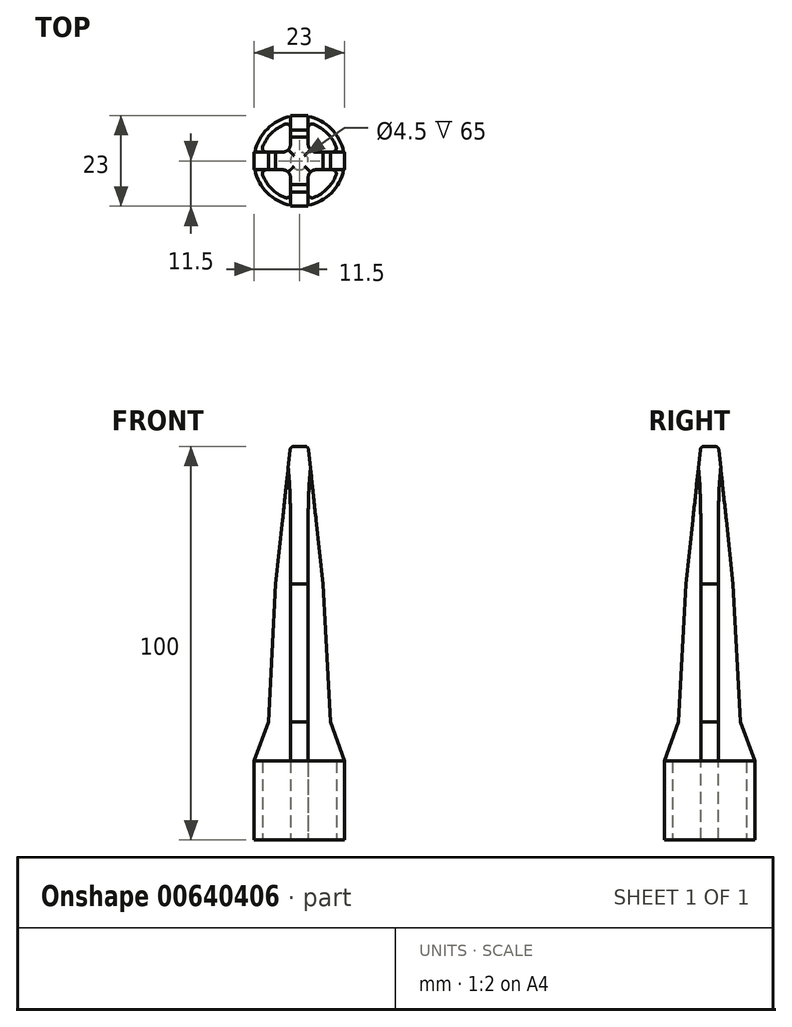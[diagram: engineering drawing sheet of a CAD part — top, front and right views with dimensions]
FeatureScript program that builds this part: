
annotation { "Feature Type Name" : "Feature", "Feature Type Description" : "" }
export const myFeature = defineFeature(function(context is Context, id is Id, definition is map)
    precondition{}
    {
        {
            var Q0;
            Q0=qCreatedBy(makeId("Top.planeOp"),FACE);
            var sketch = newSketch(context, id + "F0", { "sketchPlane" : qUnion([Q0])});
            skCircle(sketch, "E0", {"center": v(0, 0) * mm, "radius": 11.5 * mm});
            skCircle(sketch, "E1", {"center": v(0, 0) * mm, "radius": 2.25 * mm});
            skLineSegment(sketch, "E2", {"start": v(-2.25, 2.25) * mm, "end": v(-2.25, 9.74) * mm});
            skLineSegment(sketch, "E3", {"start": v(2.25, 2.25) * mm, "end": v(2.25, 9.74) * mm});
            skLineSegment(sketch, "E4", {"start": v(2.25, 2.25) * mm, "end": v(9.74, 2.25) * mm});
            skLineSegment(sketch, "E5", {"start": v(2.25, -2.25) * mm, "end": v(9.74, -2.25) * mm});
            skLineSegment(sketch, "E6.MirrorCS", {"start": v(-2.25, -2.25) * mm, "end": v(-2.25, -9.74) * mm});
            skLineSegment(sketch, "E7.MirrorCS", {"start": v(2.25, -2.25) * mm, "end": v(2.25, -9.74) * mm});
            skLineSegment(sketch, "E8.MirrorCS", {"start": v(-2.25, 2.25) * mm, "end": v(-9.74, 2.25) * mm});
            skLineSegment(sketch, "E9.MirrorCS", {"start": v(-2.25, -2.25) * mm, "end": v(-9.74, -2.25) * mm});
            skArc(sketch, "E10", {"start": v(-9.74, -2.25) * mm, "mid": v(0, -10) * mm, "end": v(9.74, -2.25) * mm});
            skPoint(sketch, "E11.orphan", {"position": v(-2.25, 11.28) * mm});
            skPoint(sketch, "E12.orphan", {"position": v(2.25, 11.28) * mm});
            skPoint(sketch, "E13.orphan", {"position": v(-11.28, 2.25) * mm});
            skPoint(sketch, "E14.orphan", {"position": v(-11.28, -2.25) * mm});
            skPoint(sketch, "E15.orphan", {"position": v(-2.25, -11.28) * mm});
            skPoint(sketch, "E16.orphan", {"position": v(2.25, -11.28) * mm});
            skPoint(sketch, "E17.orphan", {"position": v(11.28, -2.25) * mm});
            skPoint(sketch, "E18.orphan", {"position": v(11.28, 2.25) * mm});
            skArc(sketch, "E19.trimOffspring", {"start": v(9.74, 2.25) * mm, "mid": v(0, 10) * mm, "end": v(-9.74, 2.25) * mm});
            skPoint(sketch, "E20.orphan", {"position": v(-2.25, 0) * mm});
            skPoint(sketch, "E21.orphan", {"position": v(0, 2.25) * mm});
            skPoint(sketch, "E22.orphan", {"position": v(2.25, 0) * mm});
            skPoint(sketch, "E23.orphan", {"position": v(0, -2.25) * mm});
            skSolve(sketch);
        }
        {
            var Q0;
            Q0 = qSketchRegion(id + "F0", true);
            extrude(context, id + "F1", {"entities" : qUnion([Q0]), "depth" : 65 * mm, "offsetDistance" : 25 * mm});
        }
        {
            var Q0;
            Q0=makeQuery(id+"F1.opExtrude","CAP_FACE",FACE,{"disambiguationData":[OSD([sQuery(id+"F0.wireOp",EDGE,"E0"),sQuery(id+"F0.wireOp",EDGE,"E1"),sQuery(id+"F0.wireOp",EDGE,"E2"),sQuery(id+"F0.wireOp",EDGE,"E3"),sQuery(id+"F0.wireOp",EDGE,"E4"),sQuery(id+"F0.wireOp",EDGE,"E5"),sQuery(id+"F0.wireOp",EDGE,"E6.MirrorCS"),sQuery(id+"F0.wireOp",EDGE,"E7.MirrorCS"),sQuery(id+"F0.wireOp",EDGE,"E8.MirrorCS"),sQuery(id+"F0.wireOp",EDGE,"E9.MirrorCS"),sQuery(id+"F0.wireOp",EDGE,"E10"),sQuery(id+"F0.wireOp",EDGE,"E19.trimOffspring")])],"isStart":false});
            var sketch = newSketch(context, id + "F2", { "sketchPlane" : qUnion([Q0])});
            skLineSegment(sketch, "E24.0", {"start": v(-2.25, 2.25) * mm, "end": v(-2.25, 6) * mm});
            skLineSegment(sketch, "E25.0", {"start": v(-2.25, 2.25) * mm, "end": v(-6, 2.25) * mm});
            skLineSegment(sketch, "E26.0", {"start": v(-2.25, -2.25) * mm, "end": v(-6, -2.25) * mm});
            skLineSegment(sketch, "E27.0", {"start": v(2.25, 2.25) * mm, "end": v(2.25, 6) * mm});
            skLineSegment(sketch, "E28.0", {"start": v(2.25, -2.25) * mm, "end": v(6, -2.25) * mm});
            skLineSegment(sketch, "E28.1", {"start": v(2.25, -2.25) * mm, "end": v(2.25, -6) * mm});
            skLineSegment(sketch, "E28.2", {"start": v(2.25, 2.25) * mm, "end": v(6, 2.25) * mm});
            skLineSegment(sketch, "E28.3", {"start": v(-2.25, -2.25) * mm, "end": v(-2.25, -6) * mm});
            skLineSegment(sketch, "E29", {"start": v(-2.25, 6) * mm, "end": v(2.25, 6) * mm});
            skLineSegment(sketch, "E30", {"start": v(-6, 2.25) * mm, "end": v(-6, -2.25) * mm});
            skLineSegment(sketch, "E31", {"start": v(-2.25, -6) * mm, "end": v(2.25, -6) * mm});
            skLineSegment(sketch, "E32", {"start": v(6, 2.25) * mm, "end": v(6, -2.25) * mm});
            skPoint(sketch, "E33.orphan", {"position": v(-9.74, 2.25) * mm});
            skPoint(sketch, "E34.orphan", {"position": v(-9.74, -2.25) * mm});
            skPoint(sketch, "E35.orphan", {"position": v(2.25, -9.74) * mm});
            skPoint(sketch, "E36.orphan", {"position": v(-2.25, -9.74) * mm});
            skPoint(sketch, "E37.orphan", {"position": v(9.74, -2.25) * mm});
            skPoint(sketch, "E38.orphan", {"position": v(9.74, 2.25) * mm});
            skPoint(sketch, "E39.orphan", {"position": v(2.25, 9.74) * mm});
            skPoint(sketch, "E40.orphan", {"position": v(-2.25, 9.74) * mm});
            skSolve(sketch);
        }
        {
            var Q0;
            Q0 = qSketchRegion(id + "F2", true);
            extrude(context, id + "F3", {"entities" : qUnion([Q0]), "operationType" : NewBodyOperationType.ADD, "depth" : 35 * mm, "offsetDistance" : 25 * mm});
        }
        {
            var Q0;
            Q0=makeQuery(id+"F3.boolean.opBoolean","MERGE",FACE,{"derivedFrom":[makeQuery(id+"F1.opExtrude","SWEPT_FACE",FACE,{"disambiguationData":[OSD([sQuery(id+"F0.wireOp",EDGE,"E7.MirrorCS")])]}),makeQuery(id+"F3.opExtrude","SWEPT_FACE",FACE,{"disambiguationData":[OSD([sQuery(id+"F2.wireOp",EDGE,"E28.1")])]})]});
            var sketch = newSketch(context, id + "F4", { "sketchPlane" : qUnion([Q0])});
            skLineSegment(sketch, "E41.0", {"start": v(-6, 100) * mm, "end": v(-6, 65) * mm});
            skLineSegment(sketch, "E41.1", {"start": v(6, 100) * mm, "end": v(6, 65) * mm});
            skLineSegment(sketch, "E41.2", {"start": v(2.25, 100) * mm, "end": v(6, 100) * mm});
            skLineSegment(sketch, "E41.3", {"start": v(-2.25, 100) * mm, "end": v(-6, 100) * mm});
            skLineSegment(sketch, "E42", {"start": v(-2.25, 100) * mm, "end": v(-6, 65) * mm});
            skLineSegment(sketch, "E43", {"start": v(2.25, 100) * mm, "end": v(6, 65) * mm});
            skSolve(sketch);
        }
        {
            var Q0;
            Q0 = qSketchRegion(id + "F4", true);
            var Q1;
            Q1=makeQuery(id+"F3.boolean.opBoolean","MERGE",FACE,{"derivedFrom":[makeQuery(id+"F1.opExtrude","SWEPT_FACE",FACE,{"disambiguationData":[OSD([sQuery(id+"F0.wireOp",EDGE,"E2")])]}),makeQuery(id+"F3.opExtrude","SWEPT_FACE",FACE,{"disambiguationData":[OSD([sQuery(id+"F2.wireOp",EDGE,"E24.0")])]})]});
            extrude(context, id + "F5", {"entities" : qUnion([Q0]), "operationType" : NewBodyOperationType.REMOVE, "endBound" : BoundingType.UP_TO_SURFACE, "oppositeDirection" : true, "depth" : 25 * mm, "endBoundEntityFace" : qUnion([Q1]), "offsetDistance" : 25 * mm});
        }
        {
            var Q0;
            Q0=makeQuery(id+"F3.boolean.opBoolean","MERGE",FACE,{"derivedFrom":[makeQuery(id+"F1.opExtrude","SWEPT_FACE",FACE,{"disambiguationData":[OSD([sQuery(id+"F0.wireOp",EDGE,"E4")])]}),makeQuery(id+"F3.opExtrude","SWEPT_FACE",FACE,{"disambiguationData":[OSD([sQuery(id+"F2.wireOp",EDGE,"E28.2")])]})]});
            var sketch = newSketch(context, id + "F6", { "sketchPlane" : qUnion([Q0])});
            skLineSegment(sketch, "E44", {"start": v(-2.25, 100) * mm, "end": v(-6, 65) * mm});
            skLineSegment(sketch, "E45.0", {"start": v(-6, 100) * mm, "end": v(-6, 65) * mm});
            skLineSegment(sketch, "E46.0", {"start": v(-2.25, 100) * mm, "end": v(-6, 100) * mm});
            skLineSegment(sketch, "E46.1", {"start": v(2.25, 100) * mm, "end": v(6, 100) * mm});
            skLineSegment(sketch, "E46.2", {"start": v(6, 100) * mm, "end": v(6, 65) * mm});
            skLineSegment(sketch, "E47", {"start": v(2.25, 100) * mm, "end": v(6, 65) * mm});
            skSolve(sketch);
        }
        {
            var Q0;
            Q0 = qSketchRegion(id + "F6", true);
            var Q1;
            Q1=makeQuery(id+"F3.boolean.opBoolean","MERGE",FACE,{"derivedFrom":[makeQuery(id+"F1.opExtrude","SWEPT_FACE",FACE,{"disambiguationData":[OSD([sQuery(id+"F0.wireOp",EDGE,"E9.MirrorCS")])]}),makeQuery(id+"F3.opExtrude","SWEPT_FACE",FACE,{"disambiguationData":[OSD([sQuery(id+"F2.wireOp",EDGE,"E26.0")])]})]});
            extrude(context, id + "F7", {"entities" : qUnion([Q0]), "operationType" : NewBodyOperationType.REMOVE, "endBound" : BoundingType.UP_TO_SURFACE, "oppositeDirection" : true, "depth" : 25 * mm, "endBoundEntityFace" : qUnion([Q1]), "offsetDistance" : 25 * mm});
        }
        {
            var Q0;
            Q0=makeQuery(id+"F1.opExtrude","CAP_FACE",FACE,{"disambiguationData":[OSD([sQuery(id+"F0.wireOp",EDGE,"E0"),sQuery(id+"F0.wireOp",EDGE,"E1"),sQuery(id+"F0.wireOp",EDGE,"E2"),sQuery(id+"F0.wireOp",EDGE,"E3"),sQuery(id+"F0.wireOp",EDGE,"E4"),sQuery(id+"F0.wireOp",EDGE,"E5"),sQuery(id+"F0.wireOp",EDGE,"E6.MirrorCS"),sQuery(id+"F0.wireOp",EDGE,"E7.MirrorCS"),sQuery(id+"F0.wireOp",EDGE,"E8.MirrorCS"),sQuery(id+"F0.wireOp",EDGE,"E9.MirrorCS"),sQuery(id+"F0.wireOp",EDGE,"E10"),sQuery(id+"F0.wireOp",EDGE,"E19.trimOffspring")])],"isStart":false});
            var sketch = newSketch(context, id + "F8", { "sketchPlane" : qUnion([Q0])});
            skLineSegment(sketch, "E48.0", {"start": v(-2.25, 7.87) * mm, "end": v(-2.25, 9.74) * mm});
            skLineSegment(sketch, "E49.0", {"start": v(2.25, 7.87) * mm, "end": v(2.25, 9.74) * mm});
            skLineSegment(sketch, "E50.0", {"start": v(7.87, 2.25) * mm, "end": v(9.74, 2.25) * mm});
            skLineSegment(sketch, "E51.0", {"start": v(7.87, -2.25) * mm, "end": v(9.74, -2.25) * mm});
            skLineSegment(sketch, "E52.MirrorCS", {"start": v(-7.87, 2.25) * mm, "end": v(-9.74, 2.25) * mm});
            skLineSegment(sketch, "E53.MirrorCS", {"start": v(-7.87, -2.25) * mm, "end": v(-9.74, -2.25) * mm});
            skLineSegment(sketch, "E54.MirrorCS", {"start": v(-2.25, -7.87) * mm, "end": v(-2.25, -9.74) * mm});
            skLineSegment(sketch, "E55.MirrorCS", {"start": v(2.25, -7.87) * mm, "end": v(2.25, -9.74) * mm});
            skCircle(sketch, "E56.0", {"center": v(0, 0) * mm, "radius": 11.5 * mm});
            skArc(sketch, "E57.0", {"start": v(-2.25, 9.74) * mm, "mid": v(-7.07, 7.07) * mm, "end": v(-9.74, 2.25) * mm});
            skArc(sketch, "E58.0", {"start": v(9.74, 2.25) * mm, "mid": v(7.07, 7.07) * mm, "end": v(2.25, 9.74) * mm});
            skArc(sketch, "E58.1", {"start": v(2.25, -9.74) * mm, "mid": v(7.07, -7.07) * mm, "end": v(9.74, -2.25) * mm});
            skArc(sketch, "E58.2", {"start": v(-9.74, -2.25) * mm, "mid": v(-7.07, -7.07) * mm, "end": v(-2.25, -9.74) * mm});
            skLineSegment(sketch, "E59", {"start": v(-7.87, 2.25) * mm, "end": v(-7.87, -2.25) * mm});
            skLineSegment(sketch, "E60", {"start": v(-2.25, -7.87) * mm, "end": v(2.25, -7.87) * mm});
            skLineSegment(sketch, "E61", {"start": v(7.87, -2.25) * mm, "end": v(7.87, 2.25) * mm});
            skLineSegment(sketch, "E62", {"start": v(-2.25, 7.87) * mm, "end": v(2.25, 7.87) * mm});
            skPoint(sketch, "E63.orphan", {"position": v(-2.25, 6) * mm});
            skPoint(sketch, "E64.orphan", {"position": v(2.25, 6) * mm});
            skPoint(sketch, "E65.MirrorCS.end.orphan", {"position": v(-6, -2.25) * mm});
            skPoint(sketch, "E65.MirrorCS.start.orphan", {"position": v(-6, 2.25) * mm});
            skPoint(sketch, "E66.orphan", {"position": v(-2.25, -6) * mm});
            skPoint(sketch, "E67.MirrorCS.end.orphan", {"position": v(2.25, -6) * mm});
            skPoint(sketch, "E68.orphan", {"position": v(6, -2.25) * mm});
            skPoint(sketch, "E69.orphan", {"position": v(6, 2.25) * mm});
            skSolve(sketch);
        }
        {
            var Q0;
            Q0 = qSketchRegion(id + "F8", true);
            extrude(context, id + "F9", {"entities" : qUnion([Q0]), "operationType" : NewBodyOperationType.REMOVE, "oppositeDirection" : true, "depth" : 35 * mm, "offsetDistance" : 25 * mm});
        }
        {
            var Q0;
            Q0=makeQuery(id+"F3.boolean.opBoolean","MERGE",FACE,{"derivedFrom":[makeQuery(id+"F1.opExtrude","SWEPT_FACE",FACE,{"disambiguationData":[OSD([sQuery(id+"F0.wireOp",EDGE,"E9.MirrorCS")])]}),makeQuery(id+"F3.opExtrude","SWEPT_FACE",FACE,{"disambiguationData":[OSD([sQuery(id+"F2.wireOp",EDGE,"E26.0")])]})]});
            var sketch = newSketch(context, id + "F10", { "sketchPlane" : qUnion([Q0])});
            skLineSegment(sketch, "E70.0", {"start": v(-7.87, 30) * mm, "end": v(-7.87, 65) * mm});
            skLineSegment(sketch, "E71.0", {"start": v(-6, 65) * mm, "end": v(-7.87, 65) * mm});
            skLineSegment(sketch, "E72", {"start": v(-6, 65) * mm, "end": v(-7.87, 30) * mm});
            skLineSegment(sketch, "E73.MirrorCS", {"start": v(6, 65) * mm, "end": v(7.87, 30) * mm});
            skLineSegment(sketch, "E74.MirrorCS", {"start": v(6, 65) * mm, "end": v(7.87, 65) * mm});
            skLineSegment(sketch, "E75.MirrorCS", {"start": v(7.87, 30) * mm, "end": v(7.87, 65) * mm});
            skSolve(sketch);
        }
        {
            var Q0;
            Q0 = qSketchRegion(id + "F10", true);
            var Q1;
            Q1=makeQuery(id+"F3.boolean.opBoolean","MERGE",FACE,{"derivedFrom":[makeQuery(id+"F1.opExtrude","SWEPT_FACE",FACE,{"disambiguationData":[OSD([sQuery(id+"F0.wireOp",EDGE,"E4")])]}),makeQuery(id+"F3.opExtrude","SWEPT_FACE",FACE,{"disambiguationData":[OSD([sQuery(id+"F2.wireOp",EDGE,"E28.2")])]})]});
            extrude(context, id + "F11", {"entities" : qUnion([Q0]), "operationType" : NewBodyOperationType.REMOVE, "endBound" : BoundingType.UP_TO_SURFACE, "oppositeDirection" : true, "depth" : 25 * mm, "endBoundEntityFace" : qUnion([Q1]), "offsetDistance" : 25 * mm});
        }
        {
            var Q0;
            Q0=makeQuery(id+"F3.boolean.opBoolean","MERGE",FACE,{"derivedFrom":[makeQuery(id+"F1.opExtrude","SWEPT_FACE",FACE,{"disambiguationData":[OSD([sQuery(id+"F0.wireOp",EDGE,"E2")])]}),makeQuery(id+"F3.opExtrude","SWEPT_FACE",FACE,{"disambiguationData":[OSD([sQuery(id+"F2.wireOp",EDGE,"E24.0")])]})]});
            var sketch = newSketch(context, id + "F12", { "sketchPlane" : qUnion([Q0])});
            skLineSegment(sketch, "E76.0", {"start": v(-6, 65) * mm, "end": v(-7.87, 65) * mm});
            skLineSegment(sketch, "E76.1", {"start": v(6, 65) * mm, "end": v(7.87, 65) * mm});
            skLineSegment(sketch, "E76.2", {"start": v(7.87, 30) * mm, "end": v(7.87, 65) * mm});
            skLineSegment(sketch, "E76.3", {"start": v(-7.87, 30) * mm, "end": v(-7.87, 65) * mm});
            skLineSegment(sketch, "E77", {"start": v(-6, 65) * mm, "end": v(-7.87, 30) * mm});
            skLineSegment(sketch, "E78", {"start": v(6, 65) * mm, "end": v(7.87, 30) * mm});
            skSolve(sketch);
        }
        {
            var Q0;
            Q0 = qSketchRegion(id + "F12", true);
            var Q1;
            Q1=makeQuery(id+"F3.boolean.opBoolean","MERGE",FACE,{"derivedFrom":[makeQuery(id+"F1.opExtrude","SWEPT_FACE",FACE,{"disambiguationData":[OSD([sQuery(id+"F0.wireOp",EDGE,"E7.MirrorCS")])]}),makeQuery(id+"F3.opExtrude","SWEPT_FACE",FACE,{"disambiguationData":[OSD([sQuery(id+"F2.wireOp",EDGE,"E28.1")])]})]});
            extrude(context, id + "F13", {"entities" : qUnion([Q0]), "operationType" : NewBodyOperationType.REMOVE, "endBound" : BoundingType.UP_TO_SURFACE, "oppositeDirection" : true, "depth" : 25 * mm, "endBoundEntityFace" : qUnion([Q1]), "offsetDistance" : 25 * mm});
        }
        {
            var Q0;
            Q0=makeQuery(id+"F3.opExtrude","CAP_FACE",FACE,{"disambiguationData":[OSD([sQuery(id+"F2.wireOp",EDGE,"E24.0"),sQuery(id+"F2.wireOp",EDGE,"E25.0"),sQuery(id+"F2.wireOp",EDGE,"E26.0"),sQuery(id+"F2.wireOp",EDGE,"E27.0"),sQuery(id+"F2.wireOp",EDGE,"E28.0"),sQuery(id+"F2.wireOp",EDGE,"E28.1"),sQuery(id+"F2.wireOp",EDGE,"E28.2"),sQuery(id+"F2.wireOp",EDGE,"E28.3"),sQuery(id+"F2.wireOp",EDGE,"E29"),sQuery(id+"F2.wireOp",EDGE,"E30"),sQuery(id+"F2.wireOp",EDGE,"E31"),sQuery(id+"F2.wireOp",EDGE,"E32")])],"isStart":false});
            fillet(context, id + "F14", {"entities" : qUnion([Q0]), "radius" : 1 * mm, "tangentPropagation" : true, "allowEdgeOverflow" : false});
        }
        {
            var Q0;
            Q0=makeQuery(id+"F9.boolean.opBoolean","COPY",FACE,{"derivedFrom":makeQuery(id+"F9.opExtrude","CAP_FACE",FACE,{"disambiguationData":[OSD([sQuery(id+"F8.wireOp",EDGE,"E48.0"),sQuery(id+"F8.wireOp",EDGE,"E49.0"),sQuery(id+"F8.wireOp",EDGE,"E50.0"),sQuery(id+"F8.wireOp",EDGE,"E51.0"),sQuery(id+"F8.wireOp",EDGE,"E52.MirrorCS"),sQuery(id+"F8.wireOp",EDGE,"E53.MirrorCS"),sQuery(id+"F8.wireOp",EDGE,"E54.MirrorCS"),sQuery(id+"F8.wireOp",EDGE,"E55.MirrorCS"),sQuery(id+"F8.wireOp",EDGE,"E56.0"),sQuery(id+"F8.wireOp",EDGE,"E57.0"),sQuery(id+"F8.wireOp",EDGE,"E58.0"),sQuery(id+"F8.wireOp",EDGE,"E58.1"),sQuery(id+"F8.wireOp",EDGE,"E58.2"),sQuery(id+"F8.wireOp",EDGE,"E59"),sQuery(id+"F8.wireOp",EDGE,"E60"),sQuery(id+"F8.wireOp",EDGE,"E61"),sQuery(id+"F8.wireOp",EDGE,"E62")])],"isStart":false})});
            var sketch = newSketch(context, id + "F15", { "sketchPlane" : qUnion([Q0])});
            skCircle(sketch, "E79.0", {"center": v(0, 0) * mm, "radius": 11.5 * mm});
            skArc(sketch, "E80.0", {"start": v(-2.25, 9.74) * mm, "mid": v(-7.07, 7.07) * mm, "end": v(-9.74, 2.25) * mm});
            skLineSegment(sketch, "E80.1", {"start": v(-2.25, 7.87) * mm, "end": v(-2.25, 9.74) * mm});
            skLineSegment(sketch, "E80.2", {"start": v(2.25, 7.87) * mm, "end": v(2.25, 9.74) * mm});
            skArc(sketch, "E80.3", {"start": v(9.74, 2.25) * mm, "mid": v(7.07, 7.07) * mm, "end": v(2.25, 9.74) * mm});
            skLineSegment(sketch, "E80.4", {"start": v(7.87, 2.25) * mm, "end": v(9.74, 2.25) * mm});
            skLineSegment(sketch, "E80.5", {"start": v(7.87, -2.25) * mm, "end": v(9.74, -2.25) * mm});
            skArc(sketch, "E80.6", {"start": v(2.25, -9.74) * mm, "mid": v(7.07, -7.07) * mm, "end": v(9.74, -2.25) * mm});
            skLineSegment(sketch, "E80.7", {"start": v(-7.87, 2.25) * mm, "end": v(-9.74, 2.25) * mm});
            skLineSegment(sketch, "E80.8", {"start": v(-7.87, 2.25) * mm, "end": v(-7.87, -2.25) * mm});
            skLineSegment(sketch, "E80.9", {"start": v(-2.25, 7.87) * mm, "end": v(2.25, 7.87) * mm});
            skLineSegment(sketch, "E80.10", {"start": v(7.87, -2.25) * mm, "end": v(7.87, 2.25) * mm});
            skLineSegment(sketch, "E80.11", {"start": v(-2.25, -7.87) * mm, "end": v(2.25, -7.87) * mm});
            skLineSegment(sketch, "E80.12", {"start": v(2.25, -7.87) * mm, "end": v(2.25, -9.74) * mm});
            skLineSegment(sketch, "E80.13", {"start": v(-2.25, -7.87) * mm, "end": v(-2.25, -9.74) * mm});
            skArc(sketch, "E80.14", {"start": v(-9.74, -2.25) * mm, "mid": v(-7.07, -7.07) * mm, "end": v(-2.25, -9.74) * mm});
            skLineSegment(sketch, "E80.15", {"start": v(-7.87, -2.25) * mm, "end": v(-9.74, -2.25) * mm});
            skSolve(sketch);
        }
        {
            var Q0;
            Q0 = qSketchRegion(id + "F15", true);
            extrude(context, id + "F16", {"entities" : qUnion([Q0]), "operationType" : NewBodyOperationType.REMOVE, "oppositeDirection" : true, "depth" : 10 * mm, "offsetDistance" : 25 * mm});
        }
        {
            var Q0;
            Q0=makeQuery(id+"F3.boolean.opBoolean","MERGE",FACE,{"derivedFrom":[makeQuery(id+"F1.opExtrude","SWEPT_FACE",FACE,{"disambiguationData":[OSD([sQuery(id+"F0.wireOp",EDGE,"E5")])]}),makeQuery(id+"F3.opExtrude","SWEPT_FACE",FACE,{"disambiguationData":[OSD([sQuery(id+"F2.wireOp",EDGE,"E28.0")])]})]});
            var sketch = newSketch(context, id + "F17", { "sketchPlane" : qUnion([Q0])});
            skLineSegment(sketch, "E81.0", {"start": v(7.87, 20) * mm, "end": v(11.5, 20) * mm});
            skLineSegment(sketch, "E82.0", {"start": v(7.87, 20) * mm, "end": v(7.87, 30) * mm});
            skLineSegment(sketch, "E83", {"start": v(7.87, 30) * mm, "end": v(11.5, 20) * mm});
            skPoint(sketch, "E84.orphan", {"position": v(-11.5, 20) * mm});
            skLineSegment(sketch, "E85.MirrorCS", {"start": v(-7.87, 20) * mm, "end": v(-7.87, 30) * mm});
            skLineSegment(sketch, "E86.MirrorCS", {"start": v(-7.87, 30) * mm, "end": v(-11.5, 20) * mm});
            skLineSegment(sketch, "E87.MirrorCS", {"start": v(-7.87, 20) * mm, "end": v(-11.5, 20) * mm});
            skSolve(sketch);
        }
        {
            var Q0;
            Q0 = qSketchRegion(id + "F17", true);
            var Q1;
            Q1=makeQuery(id+"F3.boolean.opBoolean","MERGE",FACE,{"derivedFrom":[makeQuery(id+"F1.opExtrude","SWEPT_FACE",FACE,{"disambiguationData":[OSD([sQuery(id+"F0.wireOp",EDGE,"E4")])]}),makeQuery(id+"F3.opExtrude","SWEPT_FACE",FACE,{"disambiguationData":[OSD([sQuery(id+"F2.wireOp",EDGE,"E28.2")])]})]});
            extrude(context, id + "F18", {"entities" : qUnion([Q0]), "operationType" : NewBodyOperationType.ADD, "endBound" : BoundingType.UP_TO_SURFACE, "oppositeDirection" : true, "depth" : 25 * mm, "endBoundEntityFace" : qUnion([Q1]), "offsetDistance" : 25 * mm});
        }
        {
            var Q0;
            Q0=makeQuery(id+"F3.boolean.opBoolean","MERGE",FACE,{"derivedFrom":[makeQuery(id+"F1.opExtrude","SWEPT_FACE",FACE,{"disambiguationData":[OSD([sQuery(id+"F0.wireOp",EDGE,"E7.MirrorCS")])]}),makeQuery(id+"F3.opExtrude","SWEPT_FACE",FACE,{"disambiguationData":[OSD([sQuery(id+"F2.wireOp",EDGE,"E28.1")])]})]});
            var sketch = newSketch(context, id + "F19", { "sketchPlane" : qUnion([Q0])});
            skLineSegment(sketch, "E88.0", {"start": v(-7.87, 20) * mm, "end": v(-11.5, 20) * mm});
            skLineSegment(sketch, "E89.0", {"start": v(-7.87, 20) * mm, "end": v(-7.87, 30) * mm});
            skLineSegment(sketch, "E90", {"start": v(-7.87, 30) * mm, "end": v(-11.5, 20) * mm});
            skPoint(sketch, "E91.orphan", {"position": v(-2.25, 20) * mm});
            skLineSegment(sketch, "E92.MirrorCS", {"start": v(7.87, 30) * mm, "end": v(11.5, 20) * mm});
            skLineSegment(sketch, "E93.MirrorCS", {"start": v(7.87, 20) * mm, "end": v(7.87, 30) * mm});
            skLineSegment(sketch, "E94.MirrorCS", {"start": v(7.87, 20) * mm, "end": v(11.5, 20) * mm});
            skSolve(sketch);
        }
        {
            var Q0;
            Q0 = qSketchRegion(id + "F19", true);
            var Q1;
            Q1=makeQuery(id+"F3.boolean.opBoolean","MERGE",FACE,{"derivedFrom":[makeQuery(id+"F1.opExtrude","SWEPT_FACE",FACE,{"disambiguationData":[OSD([sQuery(id+"F0.wireOp",EDGE,"E6.MirrorCS")])]}),makeQuery(id+"F3.opExtrude","SWEPT_FACE",FACE,{"disambiguationData":[OSD([sQuery(id+"F2.wireOp",EDGE,"E28.3")])]})]});
            extrude(context, id + "F20", {"entities" : qUnion([Q0]), "operationType" : NewBodyOperationType.ADD, "endBound" : BoundingType.UP_TO_SURFACE, "oppositeDirection" : true, "depth" : 25 * mm, "endBoundEntityFace" : qUnion([Q1]), "offsetDistance" : 25 * mm});
        }
        {
            var Q0;
            Q0=makeQuery(id+"F3.boolean.opBoolean","MERGE",EDGE,{"derivedFrom":[makeQuery(id+"F1.opExtrude","SWEPT_EDGE",EDGE,{"disambiguationData":[OSD([sQuery(id+"F0.wireOp",EDGE,"E5"),sQuery(id+"F0.wireOp",EDGE,"E7.MirrorCS")])]}),makeQuery(id+"F3.opExtrude","SWEPT_EDGE",EDGE,{"disambiguationData":[OSD([sQuery(id+"F2.wireOp",EDGE,"E28.0"),sQuery(id+"F2.wireOp",EDGE,"E28.1")])]})]});
            var Q1;
            Q1=makeQuery(id+"F3.boolean.opBoolean","MERGE",EDGE,{"derivedFrom":[makeQuery(id+"F1.opExtrude","SWEPT_EDGE",EDGE,{"disambiguationData":[OSD([sQuery(id+"F0.wireOp",EDGE,"E3"),sQuery(id+"F0.wireOp",EDGE,"E4")])]}),makeQuery(id+"F3.opExtrude","SWEPT_EDGE",EDGE,{"disambiguationData":[OSD([sQuery(id+"F2.wireOp",EDGE,"E27.0"),sQuery(id+"F2.wireOp",EDGE,"E28.2")])]})]});
            var Q2;
            Q2=makeQuery(id+"F3.boolean.opBoolean","MERGE",EDGE,{"derivedFrom":[makeQuery(id+"F1.opExtrude","SWEPT_EDGE",EDGE,{"disambiguationData":[OSD([sQuery(id+"F0.wireOp",EDGE,"E2"),sQuery(id+"F0.wireOp",EDGE,"E8.MirrorCS")])]}),makeQuery(id+"F3.opExtrude","SWEPT_EDGE",EDGE,{"disambiguationData":[OSD([sQuery(id+"F2.wireOp",EDGE,"E24.0"),sQuery(id+"F2.wireOp",EDGE,"E25.0")])]})]});
            var Q3;
            Q3=makeQuery(id+"F3.boolean.opBoolean","MERGE",EDGE,{"derivedFrom":[makeQuery(id+"F1.opExtrude","SWEPT_EDGE",EDGE,{"disambiguationData":[OSD([sQuery(id+"F0.wireOp",EDGE,"E6.MirrorCS"),sQuery(id+"F0.wireOp",EDGE,"E9.MirrorCS")])]}),makeQuery(id+"F3.opExtrude","SWEPT_EDGE",EDGE,{"disambiguationData":[OSD([sQuery(id+"F2.wireOp",EDGE,"E26.0"),sQuery(id+"F2.wireOp",EDGE,"E28.3")])]})]});
            fillet(context, id + "F21", {"entities" : qUnion([Q0, Q1, Q2, Q3]), "radius" : 2 * mm, "tangentPropagation" : true, "allowEdgeOverflow" : false});
        }
        {
            var Q0;
            Q0=makeQuery(id+"F1.opExtrude","SWEPT_EDGE",EDGE,{"disambiguationData":[OSD([sQuery(id+"F0.wireOp",EDGE,"E7.MirrorCS"),sQuery(id+"F0.wireOp",EDGE,"E10")])]});
            var Q1;
            Q1=makeQuery(id+"F1.opExtrude","SWEPT_EDGE",EDGE,{"disambiguationData":[OSD([sQuery(id+"F0.wireOp",EDGE,"E5"),sQuery(id+"F0.wireOp",EDGE,"E10")])]});
            var Q2;
            Q2=makeQuery(id+"F1.opExtrude","SWEPT_EDGE",EDGE,{"disambiguationData":[OSD([sQuery(id+"F0.wireOp",EDGE,"E6.MirrorCS"),sQuery(id+"F0.wireOp",EDGE,"E10")])]});
            var Q3;
            Q3=makeQuery(id+"F1.opExtrude","SWEPT_EDGE",EDGE,{"disambiguationData":[OSD([sQuery(id+"F0.wireOp",EDGE,"E4"),sQuery(id+"F0.wireOp",EDGE,"E19.trimOffspring")])]});
            var Q4;
            Q4=makeQuery(id+"F1.opExtrude","SWEPT_EDGE",EDGE,{"disambiguationData":[OSD([sQuery(id+"F0.wireOp",EDGE,"E3"),sQuery(id+"F0.wireOp",EDGE,"E19.trimOffspring")])]});
            var Q5;
            Q5=makeQuery(id+"F1.opExtrude","SWEPT_EDGE",EDGE,{"disambiguationData":[OSD([sQuery(id+"F0.wireOp",EDGE,"E9.MirrorCS"),sQuery(id+"F0.wireOp",EDGE,"E10")])]});
            var Q6;
            Q6=makeQuery(id+"F1.opExtrude","SWEPT_EDGE",EDGE,{"disambiguationData":[OSD([sQuery(id+"F0.wireOp",EDGE,"E8.MirrorCS"),sQuery(id+"F0.wireOp",EDGE,"E19.trimOffspring")])]});
            var Q7;
            Q7=makeQuery(id+"F1.opExtrude","SWEPT_EDGE",EDGE,{"disambiguationData":[OSD([sQuery(id+"F0.wireOp",EDGE,"E2"),sQuery(id+"F0.wireOp",EDGE,"E19.trimOffspring")])]});
            fillet(context, id + "F22", {"entities" : qUnion([Q0, Q1, Q2, Q3, Q4, Q5, Q6, Q7]), "radius" : 1 * mm, "tangentPropagation" : true, "allowEdgeOverflow" : false});
        }
    });
